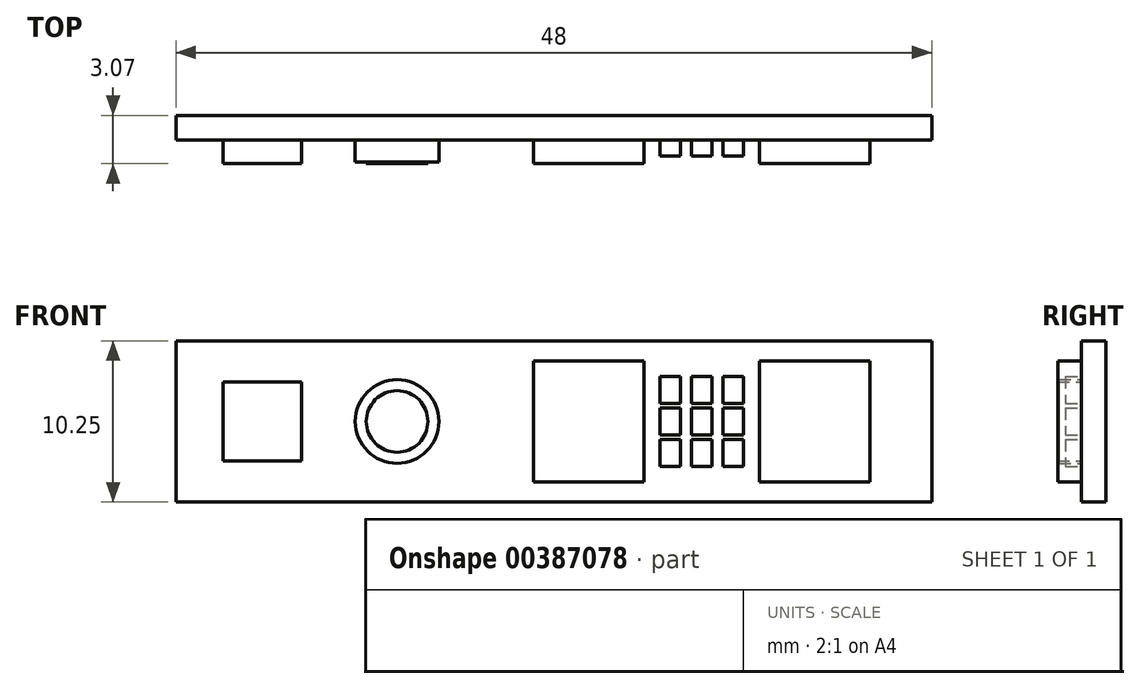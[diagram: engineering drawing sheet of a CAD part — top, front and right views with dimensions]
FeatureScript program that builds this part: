
annotation { "Feature Type Name" : "Feature", "Feature Type Description" : "" }
export const myFeature = defineFeature(function(context is Context, id is Id, definition is map)
    precondition{}
    {
        {
            var Q0;
            Q0=qCreatedBy(makeId("Front.planeOp"),FACE);
            var sketch = newSketch(context, id + "F0", { "sketchPlane" : qUnion([Q0])});
            skLineSegment(sketch, "E0.bottom", {"start": v(0, 0) * mm, "end": v(48, 0) * mm});
            skLineSegment(sketch, "E0.top", {"start": v(0, -10.25) * mm, "end": v(48, -10.25) * mm});
            skLineSegment(sketch, "E0.left", {"start": v(0, 0) * mm, "end": v(0, -10.25) * mm});
            skLineSegment(sketch, "E0.right", {"start": v(48, 0) * mm, "end": v(48, -10.25) * mm});
            skSolve(sketch);
        }
        {
            var Q0;
            Q0 = qSketchRegion(id + "F0", true);
            extrude(context, id + "F1", {"entities" : qUnion([Q0]), "depth" : 1.57 * mm});
        }
        {
            var Q0;
            Q0=makeQuery(id+"F1.opExtrude","CAP_FACE",FACE,{"disambiguationData":[OSD([sQuery(id+"F0.wireOp",EDGE,"E0.bottom"),sQuery(id+"F0.wireOp",EDGE,"E0.top"),sQuery(id+"F0.wireOp",EDGE,"E0.left"),sQuery(id+"F0.wireOp",EDGE,"E0.right")])],"isStart":false});
            var sketch = newSketch(context, id + "F2", { "sketchPlane" : qUnion([Q0])});
            skLineSegment(sketch, "E1.bottom", {"start": v(30.73, -2.28) * mm, "end": v(32.03, -2.28) * mm});
            skLineSegment(sketch, "E1.top", {"start": v(30.73, -3.98) * mm, "end": v(32.03, -3.98) * mm});
            skLineSegment(sketch, "E1.left", {"start": v(30.73, -2.28) * mm, "end": v(30.73, -3.98) * mm});
            skLineSegment(sketch, "E1.right", {"start": v(32.03, -2.28) * mm, "end": v(32.03, -3.98) * mm});
            skLineSegment(sketch, "E2", {"start": v(30.73, -3.63) * mm, "end": v(32.03, -3.63) * mm});
            skLineSegment(sketch, "E3", {"start": v(30.83, -3.63) * mm, "end": v(30.83, -2.38) * mm});
            skLineSegment(sketch, "E4", {"start": v(30.83, -2.38) * mm, "end": v(31.93, -2.38) * mm});
            skLineSegment(sketch, "E5", {"start": v(31.93, -2.38) * mm, "end": v(31.93, -3.63) * mm});
            skLineSegment(sketch, "E6.1.0.0", {"start": v(33.93, -2.38) * mm, "end": v(33.93, -3.63) * mm});
            skLineSegment(sketch, "E6.1.0.1", {"start": v(32.83, -3.63) * mm, "end": v(32.83, -2.38) * mm});
            skLineSegment(sketch, "E6.1.0.2", {"start": v(32.83, -2.38) * mm, "end": v(33.93, -2.38) * mm});
            skLineSegment(sketch, "E6.1.0.3", {"start": v(32.73, -3.63) * mm, "end": v(34.03, -3.63) * mm});
            skLineSegment(sketch, "E6.1.0.4", {"start": v(34.03, -2.28) * mm, "end": v(34.03, -3.98) * mm});
            skLineSegment(sketch, "E6.1.0.5", {"start": v(32.73, -2.28) * mm, "end": v(32.73, -3.98) * mm});
            skLineSegment(sketch, "E6.1.0.6", {"start": v(32.73, -3.98) * mm, "end": v(34.03, -3.98) * mm});
            skLineSegment(sketch, "E6.1.0.7", {"start": v(32.73, -2.28) * mm, "end": v(34.03, -2.28) * mm});
            skLineSegment(sketch, "E6.2.0.0", {"start": v(35.93, -2.38) * mm, "end": v(35.93, -3.63) * mm});
            skLineSegment(sketch, "E6.2.0.1", {"start": v(34.83, -3.63) * mm, "end": v(34.83, -2.38) * mm});
            skLineSegment(sketch, "E6.2.0.2", {"start": v(34.83, -2.38) * mm, "end": v(35.93, -2.38) * mm});
            skLineSegment(sketch, "E6.2.0.3", {"start": v(34.73, -3.63) * mm, "end": v(36.03, -3.63) * mm});
            skLineSegment(sketch, "E6.2.0.4", {"start": v(36.03, -2.28) * mm, "end": v(36.03, -3.98) * mm});
            skLineSegment(sketch, "E6.2.0.5", {"start": v(34.73, -2.28) * mm, "end": v(34.73, -3.98) * mm});
            skLineSegment(sketch, "E6.2.0.6", {"start": v(34.73, -3.98) * mm, "end": v(36.03, -3.98) * mm});
            skLineSegment(sketch, "E6.2.0.7", {"start": v(34.73, -2.28) * mm, "end": v(36.03, -2.28) * mm});
            skLineSegment(sketch, "E6.direction1", {"start": v(30.73, -3.98) * mm, "end": v(32.73, -3.98) * mm, "construction": true});
            skLineSegment(sketch, "E7.1.0.0", {"start": v(31.94, -4.38) * mm, "end": v(31.94, -5.63) * mm});
            skLineSegment(sketch, "E7.1.0.1", {"start": v(36.04, -4.28) * mm, "end": v(36.04, -5.98) * mm});
            skLineSegment(sketch, "E7.1.0.2", {"start": v(34.84, -4.38) * mm, "end": v(35.94, -4.38) * mm});
            skLineSegment(sketch, "E7.1.0.3", {"start": v(33.94, -4.38) * mm, "end": v(33.94, -5.63) * mm});
            skLineSegment(sketch, "E7.1.0.4", {"start": v(34.74, -5.98) * mm, "end": v(36.04, -5.98) * mm});
            skLineSegment(sketch, "E7.1.0.5", {"start": v(32.84, -5.63) * mm, "end": v(32.84, -4.38) * mm});
            skLineSegment(sketch, "E7.1.0.6", {"start": v(32.84, -4.38) * mm, "end": v(33.94, -4.38) * mm});
            skLineSegment(sketch, "E7.1.0.7", {"start": v(32.74, -5.63) * mm, "end": v(34.04, -5.63) * mm});
            skLineSegment(sketch, "E7.1.0.8", {"start": v(34.04, -4.28) * mm, "end": v(34.04, -5.98) * mm});
            skLineSegment(sketch, "E7.1.0.9", {"start": v(34.74, -4.28) * mm, "end": v(36.04, -4.28) * mm});
            skLineSegment(sketch, "E7.1.0.10", {"start": v(34.84, -5.63) * mm, "end": v(34.84, -4.38) * mm});
            skLineSegment(sketch, "E7.1.0.11", {"start": v(32.74, -5.98) * mm, "end": v(34.04, -5.98) * mm});
            skLineSegment(sketch, "E7.1.0.12", {"start": v(34.74, -5.63) * mm, "end": v(36.04, -5.63) * mm});
            skLineSegment(sketch, "E7.1.0.13", {"start": v(34.74, -4.28) * mm, "end": v(34.74, -5.98) * mm});
            skLineSegment(sketch, "E7.1.0.14", {"start": v(32.74, -4.28) * mm, "end": v(34.04, -4.28) * mm});
            skLineSegment(sketch, "E7.1.0.15", {"start": v(30.74, -5.98) * mm, "end": v(32.74, -5.98) * mm, "construction": true});
            skLineSegment(sketch, "E7.1.0.16", {"start": v(32.74, -4.28) * mm, "end": v(32.74, -5.98) * mm});
            skLineSegment(sketch, "E7.1.0.17", {"start": v(35.94, -4.38) * mm, "end": v(35.94, -5.63) * mm});
            skLineSegment(sketch, "E7.1.0.18", {"start": v(30.74, -4.28) * mm, "end": v(32.04, -4.28) * mm});
            skLineSegment(sketch, "E7.1.0.19", {"start": v(30.74, -4.28) * mm, "end": v(30.74, -5.98) * mm});
            skLineSegment(sketch, "E7.1.0.20", {"start": v(32.04, -4.28) * mm, "end": v(32.04, -5.98) * mm});
            skLineSegment(sketch, "E7.1.0.21", {"start": v(30.74, -5.63) * mm, "end": v(32.04, -5.63) * mm});
            skLineSegment(sketch, "E7.1.0.22", {"start": v(30.84, -5.63) * mm, "end": v(30.84, -4.38) * mm});
            skLineSegment(sketch, "E7.1.0.23", {"start": v(30.84, -4.38) * mm, "end": v(31.94, -4.38) * mm});
            skLineSegment(sketch, "E7.1.0.24", {"start": v(30.74, -5.98) * mm, "end": v(32.04, -5.98) * mm});
            skLineSegment(sketch, "E7.2.0.0", {"start": v(31.94, -6.37) * mm, "end": v(31.94, -7.62) * mm});
            skLineSegment(sketch, "E7.2.0.1", {"start": v(36.04, -6.27) * mm, "end": v(36.04, -7.97) * mm});
            skLineSegment(sketch, "E7.2.0.2", {"start": v(34.84, -6.37) * mm, "end": v(35.94, -6.37) * mm});
            skLineSegment(sketch, "E7.2.0.3", {"start": v(33.94, -6.37) * mm, "end": v(33.94, -7.62) * mm});
            skLineSegment(sketch, "E7.2.0.4", {"start": v(34.74, -7.97) * mm, "end": v(36.04, -7.97) * mm});
            skLineSegment(sketch, "E7.2.0.5", {"start": v(32.84, -7.62) * mm, "end": v(32.84, -6.37) * mm});
            skLineSegment(sketch, "E7.2.0.6", {"start": v(32.84, -6.37) * mm, "end": v(33.94, -6.37) * mm});
            skLineSegment(sketch, "E7.2.0.7", {"start": v(32.74, -7.62) * mm, "end": v(34.04, -7.62) * mm});
            skLineSegment(sketch, "E7.2.0.8", {"start": v(34.04, -6.27) * mm, "end": v(34.04, -7.97) * mm});
            skLineSegment(sketch, "E7.2.0.9", {"start": v(34.74, -6.27) * mm, "end": v(36.04, -6.27) * mm});
            skLineSegment(sketch, "E7.2.0.10", {"start": v(34.84, -7.62) * mm, "end": v(34.84, -6.37) * mm});
            skLineSegment(sketch, "E7.2.0.11", {"start": v(32.74, -7.97) * mm, "end": v(34.04, -7.97) * mm});
            skLineSegment(sketch, "E7.2.0.12", {"start": v(34.74, -7.62) * mm, "end": v(36.04, -7.62) * mm});
            skLineSegment(sketch, "E7.2.0.13", {"start": v(34.74, -6.27) * mm, "end": v(34.74, -7.97) * mm});
            skLineSegment(sketch, "E7.2.0.14", {"start": v(32.74, -6.27) * mm, "end": v(34.04, -6.27) * mm});
            skLineSegment(sketch, "E7.2.0.15", {"start": v(30.74, -7.97) * mm, "end": v(32.74, -7.97) * mm, "construction": true});
            skLineSegment(sketch, "E7.2.0.16", {"start": v(32.74, -6.27) * mm, "end": v(32.74, -7.97) * mm});
            skLineSegment(sketch, "E7.2.0.17", {"start": v(35.94, -6.37) * mm, "end": v(35.94, -7.62) * mm});
            skLineSegment(sketch, "E7.2.0.18", {"start": v(30.74, -6.27) * mm, "end": v(32.04, -6.27) * mm});
            skLineSegment(sketch, "E7.2.0.19", {"start": v(30.74, -6.27) * mm, "end": v(30.74, -7.97) * mm});
            skLineSegment(sketch, "E7.2.0.20", {"start": v(32.04, -6.27) * mm, "end": v(32.04, -7.97) * mm});
            skLineSegment(sketch, "E7.2.0.21", {"start": v(30.74, -7.62) * mm, "end": v(32.04, -7.62) * mm});
            skLineSegment(sketch, "E7.2.0.22", {"start": v(30.84, -7.62) * mm, "end": v(30.84, -6.37) * mm});
            skLineSegment(sketch, "E7.2.0.23", {"start": v(30.84, -6.37) * mm, "end": v(31.94, -6.37) * mm});
            skLineSegment(sketch, "E7.2.0.24", {"start": v(30.74, -7.97) * mm, "end": v(32.04, -7.97) * mm});
            skLineSegment(sketch, "E7.direction1", {"start": v(30.73, -3.98) * mm, "end": v(30.74, -5.98) * mm, "construction": true});
            skLineSegment(sketch, "E8.bottom", {"start": v(22.7, -1.28) * mm, "end": v(29.7, -1.28) * mm});
            skLineSegment(sketch, "E8.top", {"start": v(22.7, -8.98) * mm, "end": v(29.7, -8.98) * mm});
            skLineSegment(sketch, "E8.left", {"start": v(22.7, -1.28) * mm, "end": v(22.7, -8.98) * mm});
            skLineSegment(sketch, "E8.right", {"start": v(29.7, -1.28) * mm, "end": v(29.7, -8.98) * mm});
            skPoint(sketch, "E9.endSnap0", {"position": v(35.94, -5) * mm});
            skLineSegment(sketch, "E10", {"start": v(33.38, -2.28) * mm, "end": v(33.38, -7.97) * mm, "construction": true});
            skPoint(sketch, "E10.startSnap0", {"position": v(33.38, -2.28) * mm});
            skLineSegment(sketch, "E11", {"start": v(22.7, -5.13) * mm, "end": v(33.38, -5.13) * mm, "construction": true});
            skLineSegment(sketch, "E12.MirrorCS", {"start": v(44.06, -8.98) * mm, "end": v(37.06, -8.98) * mm});
            skLineSegment(sketch, "E13.MirrorCS", {"start": v(37.06, -1.28) * mm, "end": v(37.06, -8.98) * mm});
            skLineSegment(sketch, "E14.MirrorCS", {"start": v(44.06, -1.28) * mm, "end": v(44.06, -8.97) * mm});
            skLineSegment(sketch, "E15.MirrorCS", {"start": v(44.06, -1.28) * mm, "end": v(37.06, -1.28) * mm});
            skLineSegment(sketch, "E16.bottom", {"start": v(2.98, -2.63) * mm, "end": v(7.98, -2.63) * mm});
            skLineSegment(sketch, "E16.top", {"start": v(2.98, -7.63) * mm, "end": v(7.98, -7.63) * mm});
            skLineSegment(sketch, "E16.left", {"start": v(2.98, -2.63) * mm, "end": v(2.98, -7.63) * mm});
            skLineSegment(sketch, "E16.right", {"start": v(7.98, -2.63) * mm, "end": v(7.98, -7.63) * mm});
            skCircle(sketch, "E17", {"center": v(14.04, -5.13) * mm, "radius": 2.65 * mm});
            skLineSegment(sketch, "E18", {"start": v(22.7, -5.13) * mm, "end": v(-16.74, -5.13) * mm, "construction": true});
            skPoint(sketch, "E19", {"position": v(2.98, -5.13) * mm});
            skPoint(sketch, "E20", {"position": v(0, -5.13) * mm});
            skSolve(sketch);
        }
        {
            var Q0;
            Q0=makeQuery(id+"F2.imprint","IMPRINT",FACE,{"disambiguationData":[TD([[makeQuery(id+"F2.imprint","IMPRINT",EDGE,{"derivedFrom":sQuery(id+"F2.wireOp",EDGE,"E8.bottom")}),-1.0]])]});
            var Q1;
            Q1=makeQuery(id+"F2.imprint","IMPRINT",FACE,{"disambiguationData":[TD([[makeQuery(id+"F2.imprint","IMPRINT",EDGE,{"derivedFrom":sQuery(id+"F2.wireOp",EDGE,"E16.bottom")}),-1.0]])]});
            extrude(context, id + "F3", {"entities" : qUnion([Q0, Q1]), "depth" : 1.5 * mm});
        }
        {
            var Q0;
            Q0=makeQuery(id+"F2.imprint","IMPRINT",FACE,{"disambiguationData":[TD([[makeQuery(id+"F2.imprint","IMPRINT",EDGE,{"derivedFrom":sQuery(id+"F2.wireOp",EDGE,"E12.MirrorCS")}),-1.0]])]});
            extrude(context, id + "F4", {"entities" : qUnion([Q0]), "depth" : 1.5 * mm});
        }
        {
            var Q0;
            {var subQ1=sQuery(id+"F2.wireOp",EDGE,"E1.top");Q0=makeQuery(id+"F2.imprint","IMPRINT",FACE,{"disambiguationData":[TD([[makeQuery(id+"F2.imprint","IMPRINT",EDGE,{"derivedFrom":subQ1}),1.0]])]});}
            var Q1;
            {var subQ0=sQuery(id+"F2.wireOp",EDGE,"E3");Q1=makeQuery(id+"F2.imprint","IMPRINT",FACE,{"disambiguationData":[TD([[makeQuery(id+"F2.imprint","IMPRINT",EDGE,{"derivedFrom":subQ0}),-1.0]])]});}
            var Q2;
            {var subQ5=sQuery(id+"F2.wireOp",EDGE,"E1.bottom");Q2=makeQuery(id+"F2.imprint","IMPRINT",FACE,{"disambiguationData":[TD([[makeQuery(id+"F2.imprint","IMPRINT",EDGE,{"derivedFrom":subQ5}),-1.0]])]});}
            extrude(context, id + "F5", {"entities" : qUnion([Q0, Q1, Q2]), "depth" : 1 * mm});
        }
        {
            var Q0;
            {var subQ0=sQuery(id+"F2.wireOp",EDGE,"E6.1.0.0");Q0=makeQuery(id+"F2.imprint","IMPRINT",FACE,{"disambiguationData":[TD([[makeQuery(id+"F2.imprint","IMPRINT",EDGE,{"derivedFrom":subQ0}),-1.0]])]});}
            var Q1;
            {var subQ4=sQuery(id+"F2.wireOp",EDGE,"E6.1.0.0");Q1=makeQuery(id+"F2.imprint","IMPRINT",FACE,{"disambiguationData":[TD([[makeQuery(id+"F2.imprint","IMPRINT",EDGE,{"derivedFrom":subQ4}),1.0]])]});}
            var Q2;
            {var subQ3=sQuery(id+"F2.wireOp",EDGE,"E6.1.0.6");Q2=makeQuery(id+"F2.imprint","IMPRINT",FACE,{"disambiguationData":[TD([[makeQuery(id+"F2.imprint","IMPRINT",EDGE,{"derivedFrom":subQ3}),1.0]])]});}
            extrude(context, id + "F6", {"entities" : qUnion([Q0, Q1, Q2]), "depth" : 1 * mm});
        }
        {
            var Q0;
            {var subQ4=sQuery(id+"F2.wireOp",EDGE,"E6.2.0.0");Q0=makeQuery(id+"F2.imprint","IMPRINT",FACE,{"disambiguationData":[TD([[makeQuery(id+"F2.imprint","IMPRINT",EDGE,{"derivedFrom":subQ4}),1.0]])]});}
            var Q1;
            {var subQ0=sQuery(id+"F2.wireOp",EDGE,"E6.2.0.0");Q1=makeQuery(id+"F2.imprint","IMPRINT",FACE,{"disambiguationData":[TD([[makeQuery(id+"F2.imprint","IMPRINT",EDGE,{"derivedFrom":subQ0}),-1.0]])]});}
            var Q2;
            {var subQ3=sQuery(id+"F2.wireOp",EDGE,"E6.2.0.6");Q2=makeQuery(id+"F2.imprint","IMPRINT",FACE,{"disambiguationData":[TD([[makeQuery(id+"F2.imprint","IMPRINT",EDGE,{"derivedFrom":subQ3}),1.0]])]});}
            extrude(context, id + "F7", {"entities" : qUnion([Q0, Q1, Q2]), "depth" : 1 * mm});
        }
        {
            var Q0;
            {var subQ0=sQuery(id+"F2.wireOp",EDGE,"E7.1.0.0");Q0=makeQuery(id+"F2.imprint","IMPRINT",FACE,{"disambiguationData":[TD([[makeQuery(id+"F2.imprint","IMPRINT",EDGE,{"derivedFrom":subQ0}),-1.0]])]});}
            var Q1;
            {var subQ6=sQuery(id+"F2.wireOp",EDGE,"E7.1.0.0");Q1=makeQuery(id+"F2.imprint","IMPRINT",FACE,{"disambiguationData":[TD([[makeQuery(id+"F2.imprint","IMPRINT",EDGE,{"derivedFrom":subQ6}),1.0]])]});}
            var Q2;
            {var subQ5=sQuery(id+"F2.wireOp",EDGE,"E7.1.0.24");Q2=makeQuery(id+"F2.imprint","IMPRINT",FACE,{"disambiguationData":[TD([[makeQuery(id+"F2.imprint","IMPRINT",EDGE,{"derivedFrom":subQ5}),1.0]])]});}
            extrude(context, id + "F8", {"entities" : qUnion([Q0, Q1, Q2]), "depth" : 1 * mm});
        }
        {
            var Q0;
            {var subQ4=sQuery(id+"F2.wireOp",EDGE,"E7.1.0.3");Q0=makeQuery(id+"F2.imprint","IMPRINT",FACE,{"disambiguationData":[TD([[makeQuery(id+"F2.imprint","IMPRINT",EDGE,{"derivedFrom":subQ4}),1.0]])]});}
            var Q1;
            {var subQ0=sQuery(id+"F2.wireOp",EDGE,"E7.1.0.3");Q1=makeQuery(id+"F2.imprint","IMPRINT",FACE,{"disambiguationData":[TD([[makeQuery(id+"F2.imprint","IMPRINT",EDGE,{"derivedFrom":subQ0}),-1.0]])]});}
            var Q2;
            {var subQ3=sQuery(id+"F2.wireOp",EDGE,"E7.1.0.11");Q2=makeQuery(id+"F2.imprint","IMPRINT",FACE,{"disambiguationData":[TD([[makeQuery(id+"F2.imprint","IMPRINT",EDGE,{"derivedFrom":subQ3}),1.0]])]});}
            extrude(context, id + "F9", {"entities" : qUnion([Q0, Q1, Q2]), "depth" : 1 * mm});
        }
        {
            var Q0;
            Q0=makeQuery(id+"F2.imprint","IMPRINT",FACE,{"disambiguationData":[TD([[makeQuery(id+"F2.imprint","IMPRINT",EDGE,{"derivedFrom":sQuery(id+"F2.wireOp",EDGE,"E7.1.0.2")}),-1.0]])]});
            var Q1;
            Q1=makeQuery(id+"F2.imprint","IMPRINT",FACE,{"disambiguationData":[TD([[makeQuery(id+"F2.imprint","IMPRINT",EDGE,{"derivedFrom":sQuery(id+"F2.wireOp",EDGE,"E7.1.0.2")}),1.0]])]});
            var Q2;
            {var subQ4=sQuery(id+"F2.wireOp",EDGE,"E7.1.0.4");Q2=makeQuery(id+"F2.imprint","IMPRINT",FACE,{"disambiguationData":[TD([[makeQuery(id+"F2.imprint","IMPRINT",EDGE,{"derivedFrom":subQ4}),1.0]])]});}
            extrude(context, id + "F10", {"entities" : qUnion([Q0, Q1, Q2]), "depth" : 1 * mm});
        }
        {
            var Q0;
            {var subQ6=sQuery(id+"F2.wireOp",EDGE,"E7.2.0.0");Q0=makeQuery(id+"F2.imprint","IMPRINT",FACE,{"disambiguationData":[TD([[makeQuery(id+"F2.imprint","IMPRINT",EDGE,{"derivedFrom":subQ6}),1.0]])]});}
            var Q1;
            {var subQ0=sQuery(id+"F2.wireOp",EDGE,"E7.2.0.0");Q1=makeQuery(id+"F2.imprint","IMPRINT",FACE,{"disambiguationData":[TD([[makeQuery(id+"F2.imprint","IMPRINT",EDGE,{"derivedFrom":subQ0}),-1.0]])]});}
            var Q2;
            {var subQ5=sQuery(id+"F2.wireOp",EDGE,"E7.2.0.24");Q2=makeQuery(id+"F2.imprint","IMPRINT",FACE,{"disambiguationData":[TD([[makeQuery(id+"F2.imprint","IMPRINT",EDGE,{"derivedFrom":subQ5}),1.0]])]});}
            extrude(context, id + "F11", {"entities" : qUnion([Q0, Q1, Q2]), "depth" : 1 * mm});
        }
        {
            var Q0;
            {var subQ0=sQuery(id+"F2.wireOp",EDGE,"E7.2.0.3");Q0=makeQuery(id+"F2.imprint","IMPRINT",FACE,{"disambiguationData":[TD([[makeQuery(id+"F2.imprint","IMPRINT",EDGE,{"derivedFrom":subQ0}),-1.0]])]});}
            var Q1;
            {var subQ4=sQuery(id+"F2.wireOp",EDGE,"E7.2.0.3");Q1=makeQuery(id+"F2.imprint","IMPRINT",FACE,{"disambiguationData":[TD([[makeQuery(id+"F2.imprint","IMPRINT",EDGE,{"derivedFrom":subQ4}),1.0]])]});}
            var Q2;
            {var subQ3=sQuery(id+"F2.wireOp",EDGE,"E7.2.0.11");Q2=makeQuery(id+"F2.imprint","IMPRINT",FACE,{"disambiguationData":[TD([[makeQuery(id+"F2.imprint","IMPRINT",EDGE,{"derivedFrom":subQ3}),1.0]])]});}
            extrude(context, id + "F12", {"entities" : qUnion([Q0, Q1, Q2]), "depth" : 1 * mm});
        }
        {
            var Q0;
            {var subQ4=sQuery(id+"F2.wireOp",EDGE,"E7.2.0.4");Q0=makeQuery(id+"F2.imprint","IMPRINT",FACE,{"disambiguationData":[TD([[makeQuery(id+"F2.imprint","IMPRINT",EDGE,{"derivedFrom":subQ4}),1.0]])]});}
            var Q1;
            Q1=makeQuery(id+"F2.imprint","IMPRINT",FACE,{"disambiguationData":[TD([[makeQuery(id+"F2.imprint","IMPRINT",EDGE,{"derivedFrom":sQuery(id+"F2.wireOp",EDGE,"E7.2.0.2")}),1.0]])]});
            var Q2;
            Q2=makeQuery(id+"F2.imprint","IMPRINT",FACE,{"disambiguationData":[TD([[makeQuery(id+"F2.imprint","IMPRINT",EDGE,{"derivedFrom":sQuery(id+"F2.wireOp",EDGE,"E7.2.0.2")}),-1.0]])]});
            extrude(context, id + "F13", {"entities" : qUnion([Q0, Q1, Q2]), "depth" : 1 * mm});
        }
        {
            var Q0;
            Q0=makeQuery(id+"F2.imprint","IMPRINT",FACE,{"disambiguationData":[TD([[makeQuery(id+"F2.imprint","IMPRINT",EDGE,{"derivedFrom":sQuery(id+"F2.wireOp",EDGE,"E17")}),1.0]])]});
            extrude(context, id + "F14", {"entities" : qUnion([Q0]), "depth" : 1.4 * mm});
        }
        {
            var Q0;
            Q0=makeQuery(id+"F14.opExtrude","CAP_FACE",FACE,{"disambiguationData":[OSD([sQuery(id+"F2.wireOp",EDGE,"E17")])],"isStart":false});
            var sketch = newSketch(context, id + "F15", { "sketchPlane" : qUnion([Q0])});
            skCircle(sketch, "E21", {"center": v(14.04, -5.13) * mm, "radius": 1.96 * mm});
            skSolve(sketch);
        }
        {
            var Q0;
            Q0=makeQuery(id+"F15.imprint","IMPRINT",FACE,{"disambiguationData":[TD([[makeQuery(id+"F15.imprint","IMPRINT",EDGE,{"derivedFrom":sQuery(id+"F15.wireOp",EDGE,"E21")}),1.0]])]});
            extrude(context, id + "F16", {"entities" : qUnion([Q0]), "depth" : .1 * mm});
        }
    });
